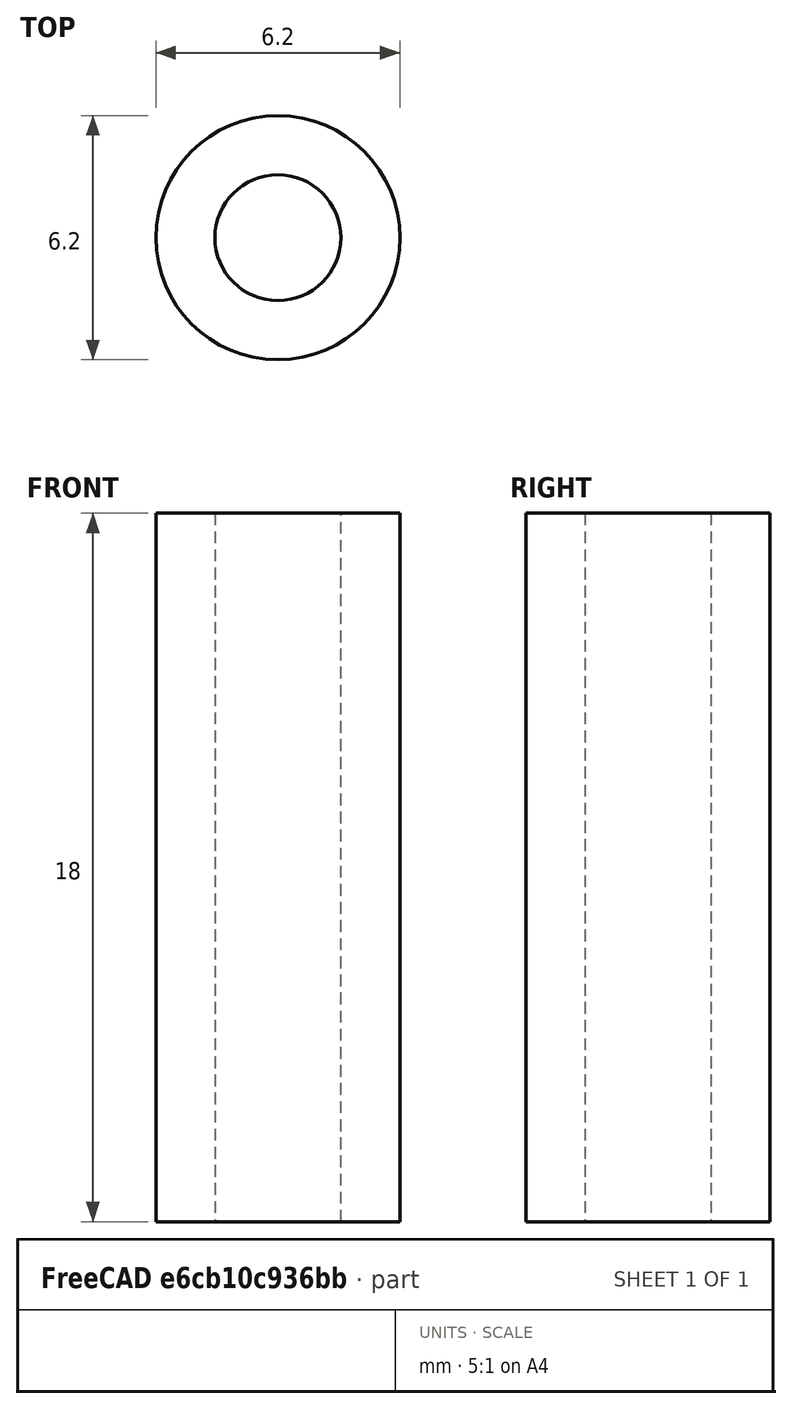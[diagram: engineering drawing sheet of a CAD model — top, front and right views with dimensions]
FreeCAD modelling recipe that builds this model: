
FCSTD DOCUMENT  (FreeCAD 0.20R29603 (Git))
Label: 6200-3200-18000
License: All rights reserved
LicenseURL: http://en.wikipedia.org/wiki/All_rights_reserved
objects: Sketcher::SketchObject×1, PartDesign::Pad×1, PartDesign::Body×1
note: 4 computed .brp shape members not serialized (recipe doc carries the construction recipe); baked Part::Feature solids carry a one-line shape summary decoded from their .brp

FEATURE [Sketcher::SketchObject] Sketch
  FullyConstrained = true
  MapMode = 5
  Support = -> [XY_Plane]
  sketch-geometry (4):
    g0: Circle CenterX=0 CenterY=0 CenterZ=0 NormalX=0 NormalY=0 NormalZ=1 AngleXU=0 Radius=3.1
    g1: Circle CenterX=0 CenterY=0 CenterZ=0 NormalX=0 NormalY=0 NormalZ=1 AngleXU=0 Radius=1.6
    g2: GeomPoint X=3.1 Y=0 Z=0
    g3: GeomPoint X=1.6 Y=0 Z=0
  constraints (9):
    c: Coincident(g0,g-1)
    c: Coincident(g1,g0)
    c: Radius(g1) = 1.6
    c: PointOnObject(g3,g1)
    c: PointOnObject(g3,g-1)
    c: PointOnObject(g2,g0)
    c: PointOnObject(g2,g-1)
    c: DistanceX(g3,g2) = 1.5
    c: Radius(g0) = 3.1
FEATURE [PartDesign::Pad] Pad
  Direction = (0,0,1)
  Length = 18
  Length2 = 10
  Profile = -> Sketch
  ReferenceAxis = -> Sketch [N_Axis]
  Type = 0
FEATURE [PartDesign::Body] Body
  Group = -> [Sketch,Pad]
  Origin = -> Origin
  Tip = -> Pad
